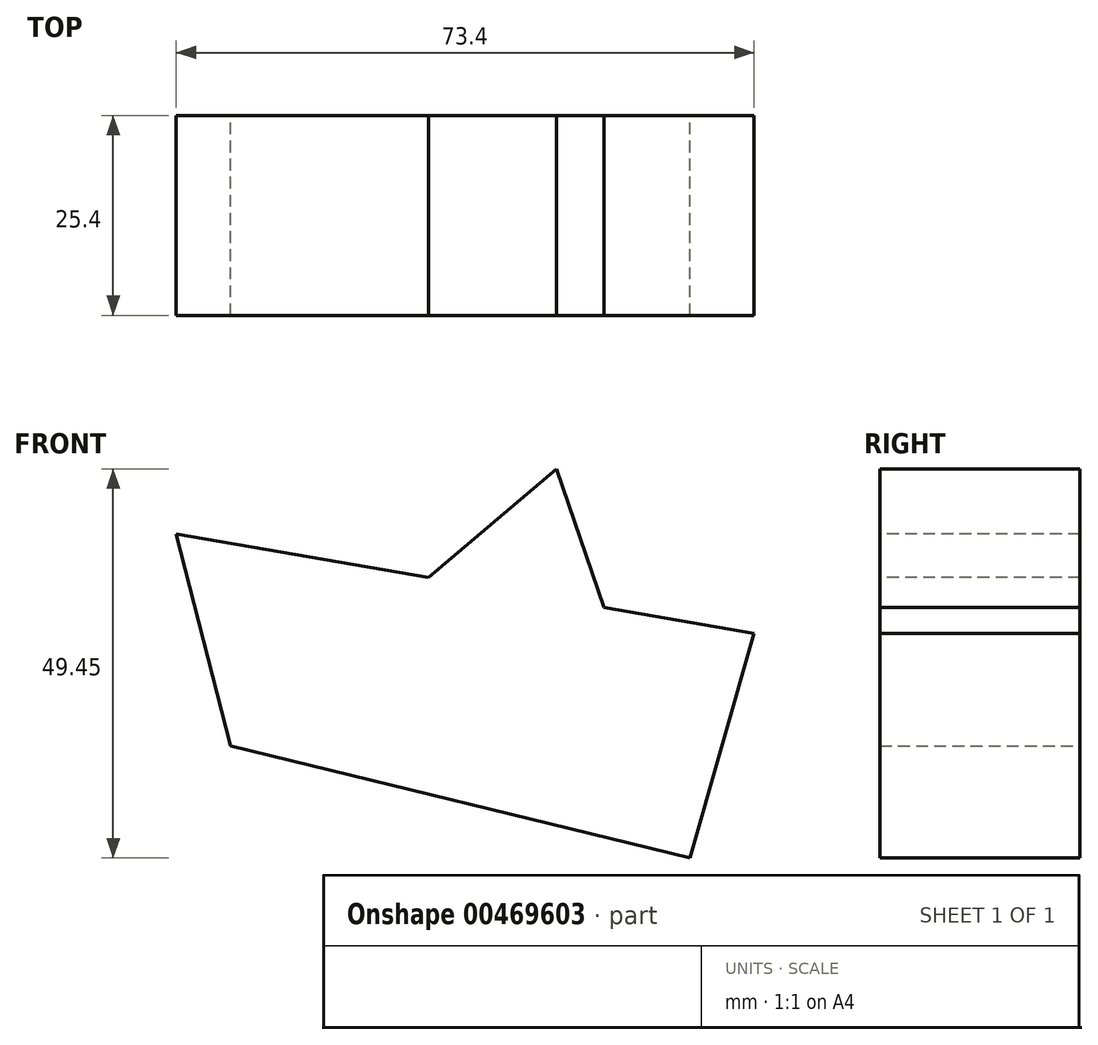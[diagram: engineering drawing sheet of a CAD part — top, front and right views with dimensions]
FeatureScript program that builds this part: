
annotation { "Feature Type Name" : "Feature", "Feature Type Description" : "" }
export const myFeature = defineFeature(function(context is Context, id is Id, definition is map)
    precondition{}
    {
        {
            var Q0;
            Q0=qCreatedBy(makeId("Front.planeOp"),FACE);
            var sketch = newSketch(context, id + "F0", { "sketchPlane" : qUnion([Q0])});
            skLineSegment(sketch, "E0", {"start": v(0, 0) * mm, "end": v(-58.37, 14.24) * mm});
            skLineSegment(sketch, "E1", {"start": v(-58.37, 14.24) * mm, "end": v(-16.96, 49.45) * mm});
            skLineSegment(sketch, "E2", {"start": v(-16.96, 49.45) * mm, "end": v(0, 0) * mm});
            skSolve(sketch);
        }
        {
            var Q0;
            Q0 = qSketchRegion(id + "F0", true);
            extrude(context, id + "F1", {"entities" : qUnion([Q0]), "depth" : 25.4 * mm});
        }
        {
            var Q0;
            Q0=makeQuery(id+"F1.opExtrude","CAP_FACE",FACE,{"disambiguationData":[OSD([sQuery(id+"F0.wireOp",EDGE,"E0"),sQuery(id+"F0.wireOp",EDGE,"E1"),sQuery(id+"F0.wireOp",EDGE,"E2")])],"isStart":false});
            var sketch = newSketch(context, id + "F2", { "sketchPlane" : qUnion([Q0])});
            skLineSegment(sketch, "E3", {"start": v(-65.25, 41.17) * mm, "end": v(8.15, 28.53) * mm});
            skLineSegment(sketch, "E4", {"start": v(8.15, 28.53) * mm, "end": v(0, 0) * mm});
            skLineSegment(sketch, "E5", {"start": v(0, 0) * mm, "end": v(-58.37, 14.24) * mm});
            skLineSegment(sketch, "E6", {"start": v(-58.37, 14.24) * mm, "end": v(-65.25, 41.17) * mm});
            skSolve(sketch);
        }
        {
            var Q0;
            Q0 = qSketchRegion(id + "F2", true);
            extrude(context, id + "F3", {"entities" : qUnion([Q0]), "operationType" : NewBodyOperationType.ADD, "oppositeDirection" : true, "depth" : 25.4 * mm});
        }
    });
